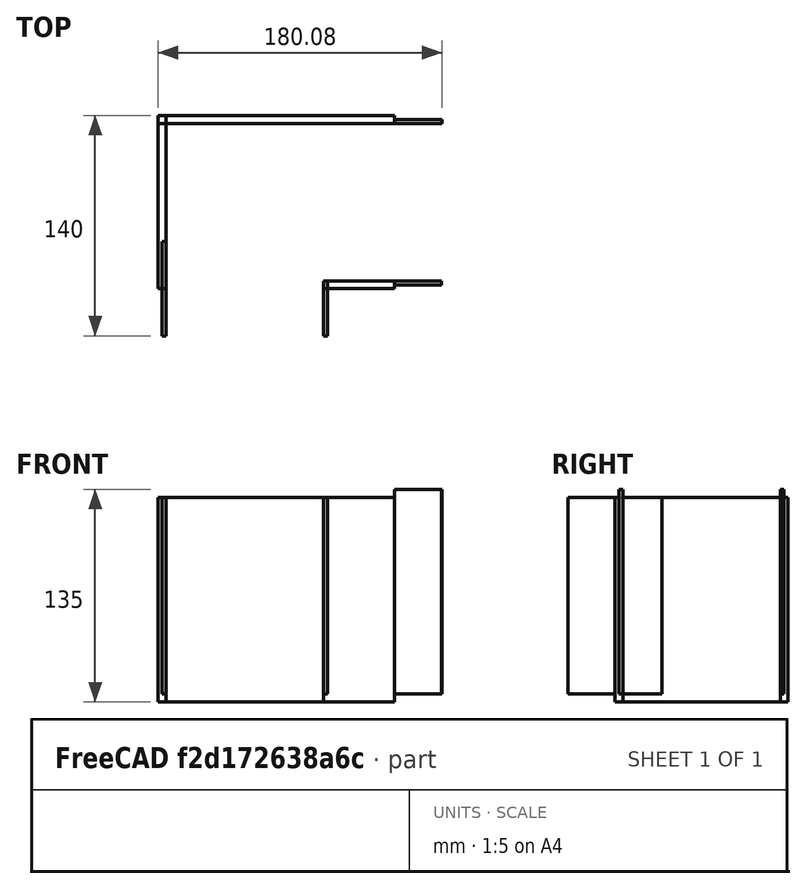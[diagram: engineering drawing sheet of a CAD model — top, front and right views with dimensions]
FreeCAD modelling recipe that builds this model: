
FCSTD DOCUMENT  (FreeCAD 0.19R24291 (Git))
Label: w maze left corner
License: All rights reserved
LicenseURL: http://en.wikipedia.org/wiki/All_rights_reserved
objects: Part::Box×7, App::MeasureDistance×1
note: 7 computed .brp shape members not serialized (recipe doc carries the construction recipe); baked Part::Feature solids carry a one-line shape summary decoded from their .brp

FEATURE [Part::Box] Box010  label="Cube010"
  AttacherType = Attacher::AttachEngine3D
  Height = 125
  Length = 2.5
  Placement = pos=(105,-30,5) rot=(0,0,1;0rad)
  Width = 35
FEATURE [Part::Box] Box009  label="Cube009"
  AttacherType = Attacher::AttachEngine3D
  Height = 125
  Length = 2.5
  Placement = pos=(2.5,-30,5) rot=(0,0,1;0rad)
  Width = 60
FEATURE [Part::Box] Box004  label="Cube004"
  AttacherType = Attacher::AttachEngine3D
  Height = 130
  Length = 5
  Width = 110
FEATURE [Part::Box] Box002  label="Cube002"
  AttacherType = Attacher::AttachEngine3D
  Height = 130
  Length = 150
  Placement = pos=(0,105,0) rot=(0,0,1;0rad)
  Width = 5
FEATURE [Part::Box] Box003  label="Cube003"
  AttacherType = Attacher::AttachEngine3D
  Height = 130
  Length = 45
  Placement = pos=(105,0,0) rot=(0,0,1;0rad)
  Width = 5
FEATURE [Part::Box] Box006  label="Cube006"
  AttacherType = Attacher::AttachEngine3D
  Height = 130
  Length = 30
  Placement = pos=(149.988,2.49023,5) rot=(0,0,1;0rad)
  Width = 2.5
FEATURE [Part::Box] Box007  label="Cube007"
  AttacherType = Attacher::AttachEngine3D
  Height = 130
  Length = 30
  Placement = pos=(150.083,104.985,5) rot=(0,0,1;0rad)
  Width = 2.5
FEATURE [App::MeasureDistance] Distance  label="Distance: 125.00 mm"
  Distance = 125
  P1 = (240,0,5)
  P2 = (240,0,130)
